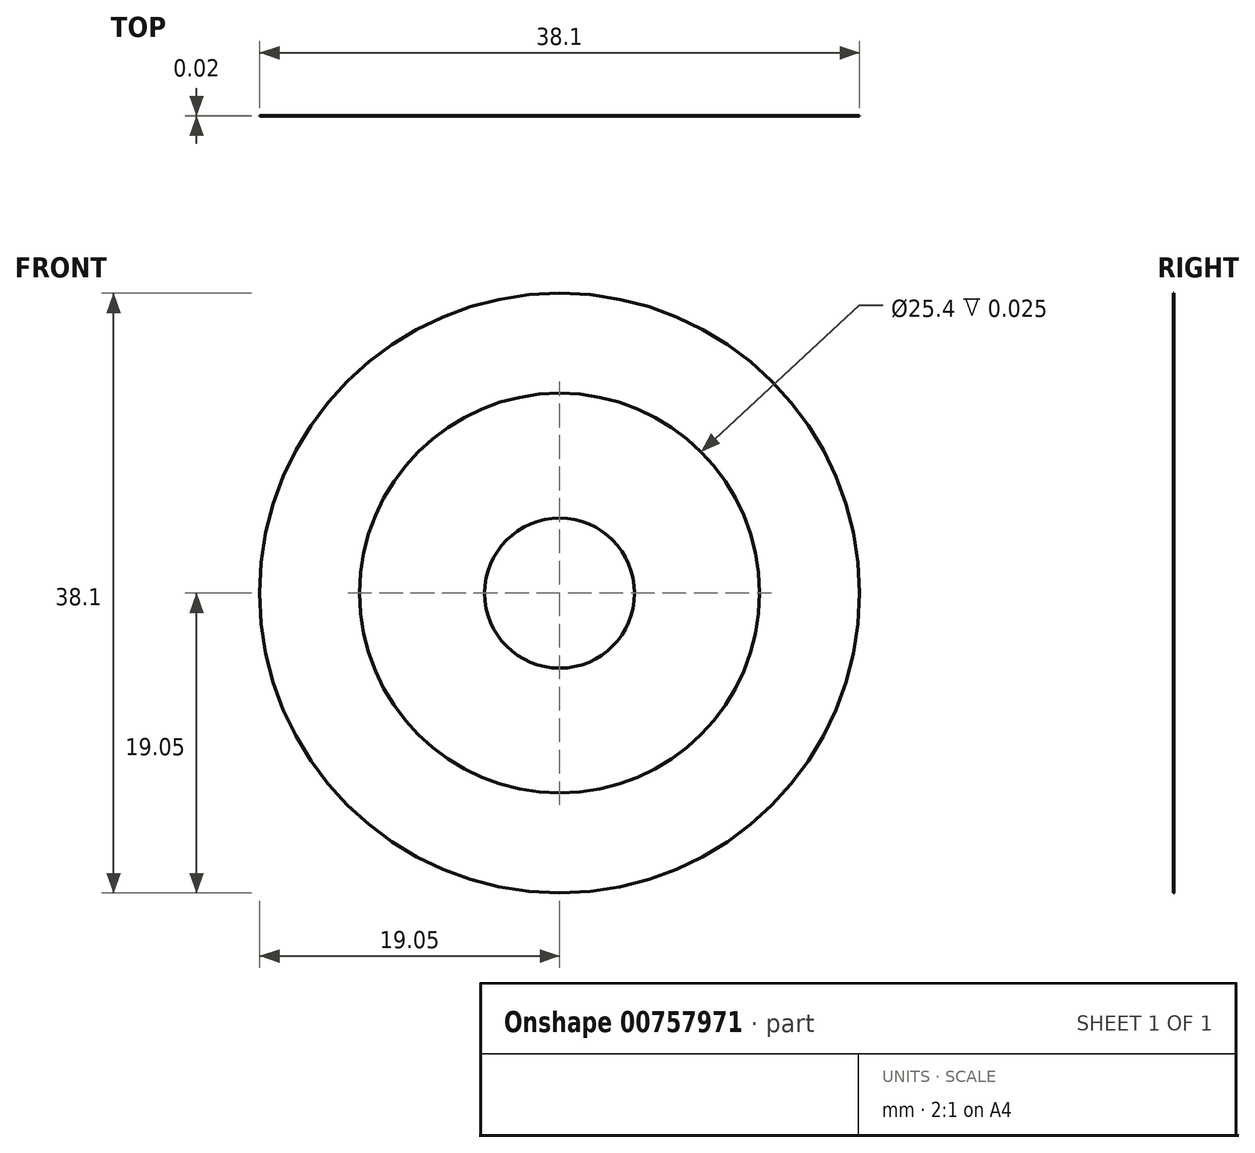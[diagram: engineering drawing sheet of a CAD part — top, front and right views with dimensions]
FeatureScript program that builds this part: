
annotation { "Feature Type Name" : "Feature", "Feature Type Description" : "" }
export const myFeature = defineFeature(function(context is Context, id is Id, definition is map)
    precondition{}
    {
        {
            var Q0;
            Q0=qCreatedBy(makeId("Front.planeOp"),FACE);
            var sketch = newSketch(context, id + "F0", { "sketchPlane" : qUnion([Q0])});
            skCircle(sketch, "E0", {"center": v(0, 0) * mm, "radius": 19.05 * mm});
            skCircle(sketch, "E1", {"center": v(0, 0) * mm, "radius": 12.7 * mm});
            skCircle(sketch, "E2", {"center": v(0, 0) * mm, "radius": 4.76 * mm});
            skSolve(sketch);
        }
        {
            var Q0;
            Q0 = qSketchRegion(id + "F0", true);
            var Q1;
            Q1=makeQuery(id+"F0.imprint","IMPRINT",FACE,{"disambiguationData":[TD([[makeQuery(id+"F0.imprint","IMPRINT",EDGE,{"derivedFrom":sQuery(id+"F0.wireOp",EDGE,"E2")}),1.0]])]});
            extrude(context, id + "F1", {"entities" : qUnion([Q0, Q1]), "endBound" : BoundingType.SYMMETRIC, "depth" : 5 / 203.2 * mm, "offsetDistance" : 25.4 * mm});
        }
    });
